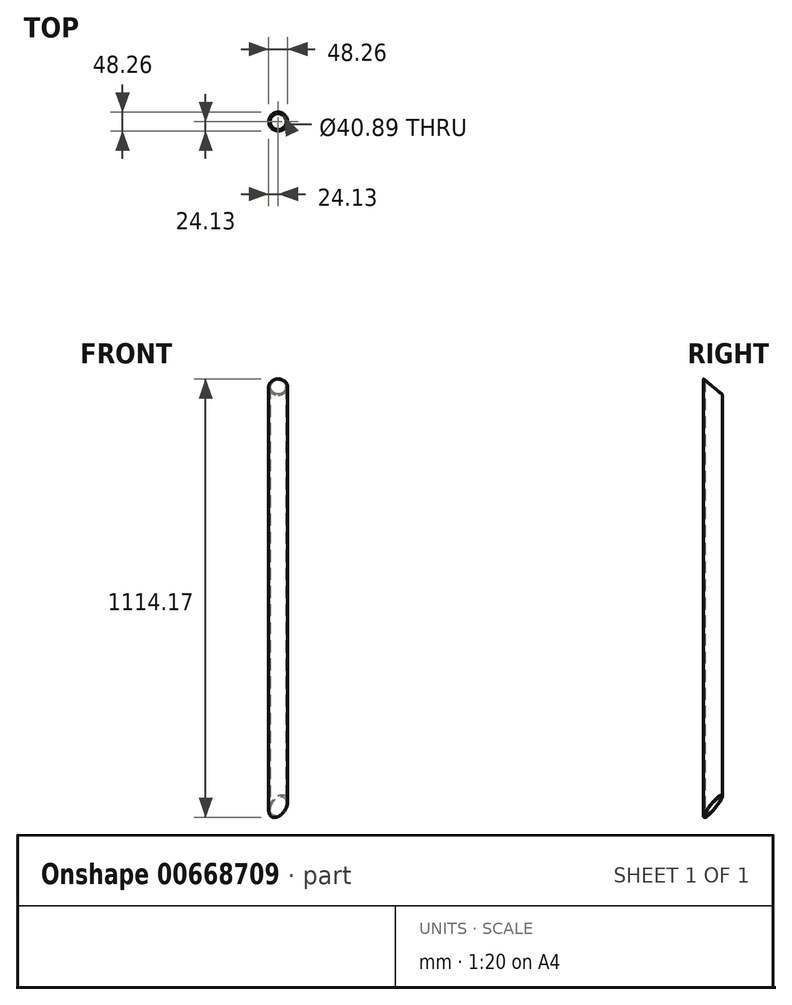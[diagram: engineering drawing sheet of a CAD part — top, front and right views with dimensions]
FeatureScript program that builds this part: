
annotation { "Feature Type Name" : "Feature", "Feature Type Description" : "" }
export const myFeature = defineFeature(function(context is Context, id is Id, definition is map)
    precondition{}
    {
        {
            var Q0;
            Q0=qCreatedBy(makeId("Top.planeOp"),FACE);
            var sketch = newSketch(context, id + "F0", { "sketchPlane" : qUnion([Q0])});
            skCircle(sketch, "E0", {"center": v(0, 0) * mm, "radius": 20.45 * mm});
            skCircle(sketch, "E1.0", {"center": v(0, 0) * mm, "radius": 24.13 * mm});
            skSolve(sketch);
        }
        {
            var Q0;
            Q0=qSketchRegion(id+"F0",true);
            extrude(context, id + "F1", {"entities" : qUnion([Q0]), "depth" : 1130.3 * mm, "offsetDistance" : 25.4 * mm});
        }
        {
            var Q0;
            Q0=qCreatedBy(makeId("Right.planeOp"),FACE);
            var sketch = newSketch(context, id + "F2", { "sketchPlane" : qUnion([Q0])});
            skLineSegment(sketch, "E2.bottom", {"start": v(24.13, 1130.3) * mm, "end": v(-24.13, 1130.3) * mm});
            skLineSegment(sketch, "E2.left", {"start": v(24.13, 1130.3) * mm, "end": v(24.13, 1089.8) * mm});
            skPoint(sketch, "E2.middle", {"position": v(0, 1110.05) * mm});
            skLineSegment(sketch, "E3", {"start": v(-24.13, 1130.3) * mm, "end": v(24.13, 1089.8) * mm});
            skPoint(sketch, "E2.top.end.orphan", {"position": v(-24.13, 1089.8) * mm});
            skSolve(sketch);
        }
        {
            var Q0;
            Q0=qSketchRegion(id+"F2",true);
            extrude(context, id + "F3", {"entities" : qUnion([Q0]), "operationType" : NewBodyOperationType.REMOVE, "endBound" : BoundingType.THROUGH_ALL, "oppositeDirection" : true, "depth" : 25.4 * mm, "hasSecondDirection" : true, "secondDirectionBound" : SecondDirectionBoundingType.THROUGH_ALL, "secondDirectionOppositeDirection" : false, "secondDirectionDepth" : 25.4 * mm});
        }
        {
            var Q0;
            Q0=qCreatedBy(makeId("Front.planeOp"),FACE);
            var sketch = newSketch(context, id + "F4", { "sketchPlane" : qUnion([Q0])});
            skLineSegment(sketch, "E4.top", {"start": v(28.58, 0) * mm, "end": v(-28.58, 0) * mm});
            skLineSegment(sketch, "E4.left", {"start": v(28.57, 26.65) * mm, "end": v(28.58, 0) * mm});
            skPoint(sketch, "E4.middle", {"position": v(0, 13.32) * mm});
            skLineSegment(sketch, "E5", {"start": v(-28.58, 0) * mm, "end": v(28.58, 26.65) * mm});
            skPoint(sketch, "E4.right.start.orphan", {"position": v(-28.58, 26.65) * mm});
            skSolve(sketch);
        }
        {
            var Q0;
            Q0=qSketchRegion(id+"F4",true);
            extrude(context, id + "F5", {"entities" : qUnion([Q0]), "operationType" : NewBodyOperationType.REMOVE, "endBound" : BoundingType.THROUGH_ALL, "depth" : 25.4 * mm, "hasSecondDirection" : true, "secondDirectionBound" : SecondDirectionBoundingType.THROUGH_ALL, "secondDirectionOppositeDirection" : true, "secondDirectionDepth" : 25.4 * mm, "offsetDistance" : 25.4 * mm});
        }
        {
            var Q0;
            Q0=makeQuery(id+"F5.boolean.opBoolean","COPY",FACE,{"derivedFrom":makeQuery(id+"F5.opExtrude","SWEPT_FACE",FACE,{"disambiguationData":[OSD([sQuery(id+"F4.wireOp",EDGE,"E5")])]})});
            var sketch = newSketch(context, id + "F6", { "sketchPlane" : qUnion([Q0])});
            skLineSegment(sketch, "E6", {"start": v(-16.93, 0) * mm, "end": v(28.2, 0) * mm});
            skSolve(sketch);
        }
        {
            var Q0;
            Q0=sQuery(id+"F6.wireOp",EDGE,"E6");
            cPlane(context, id + "F7", {"entities" : qUnion([Q0]), "cplaneType" : CPlaneType.LINE_ANGLE, "offset" : 25.4 * mm, "angle" : 45 * degree, "oppositeDirection" : true, "width" : 152.4 * mm, "height" : 152.4 * mm});
        }
        {
            var Q0;
            Q0=qCreatedBy(id+"F7.planeOp",FACE);
            var sketch = newSketch(context, id + "F8", { "sketchPlane" : qUnion([Q0])});
            skLineSegment(sketch, "E7.bottom", {"start": v(-106, -71.8) * mm, "end": v(124.4, -71.8) * mm});
            skLineSegment(sketch, "E7.top", {"start": v(-106, 106.03) * mm, "end": v(124.4, 106.03) * mm});
            skLineSegment(sketch, "E7.left", {"start": v(-106, -71.8) * mm, "end": v(-106, 106.03) * mm});
            skLineSegment(sketch, "E7.right", {"start": v(124.4, -71.8) * mm, "end": v(124.4, 106.03) * mm});
            skPoint(sketch, "E7.middle", {"position": v(9.2, 17.12) * mm});
            skSolve(sketch);
        }
        {
            var Q0;
            Q0=qSketchRegion(id+"F8",true);
            extrude(context, id + "F9", {"entities" : qUnion([Q0]), "operationType" : NewBodyOperationType.REMOVE, "depth" : 25.4 * mm, "hasSecondDirection" : true, "secondDirectionOppositeDirection" : true, "secondDirectionDepth" : 20.32 * mm, "offsetDistance" : 25.4 * mm});
        }
    });
